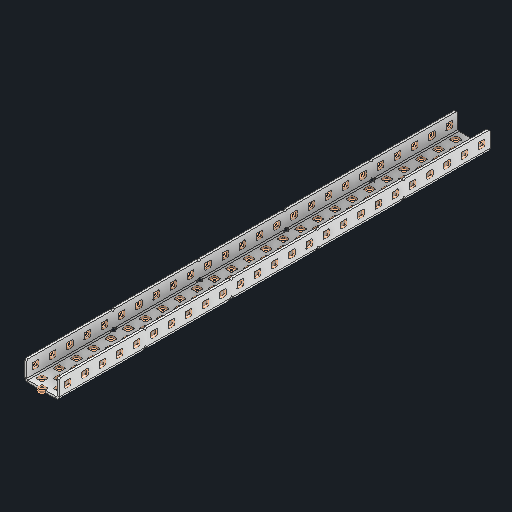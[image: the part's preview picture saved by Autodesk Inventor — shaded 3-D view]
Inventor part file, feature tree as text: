
AUTODESK INVENTOR PART (.ipt)
format: ipt  version: 2024 (Build 280153000, 153)  size: 2,044,928 bytes
history: native  units: in
note: dims shown in document units (in); Inventor stores cm internally (conversion verified against a paired STEP export)
features: other x256, sketch x5, sheet_metal_op x1
ambient origin geometry x8: Origin, YZ Plane, XZ Plane, XY Plane, X Axis, Y Axis, Z Axis, Center Point
bodies: Solid1 (feature_tree)
feature tree (262):
  other  "Alu C 1x2x1x25.ipt"
  other  "Solid1::Alu C 1x2x1x25.ipt"
  other  "TaggingFeature1"
  sketch  "Sketch1"  dims[d0=0.3937in]
  sketch  "Sketch2"  dims[d1=0.0625in]
  sketch  "Sketch3"
  other  "Flange Pattern Sketch"
  sketch  "Sketch9"
  sheet_metal_op  "Body Pattern Sketch"
  other  "Arc Length"
  sketch  "Sketch14"
  other  "Flange Pattern Plane"
  other  "Srf1"
  other  "Srf2"
  other  "Srf3"
  other  "Srf4"
  other  "Srf5"
  other  "Srf6"
  other  "Srf7"
  other  "Srf8"
  other  "Srf9"
  other  "Srf10"
  other  "Srf11"
  other  "Srf12"
  other  "Srf13"
  other  "Srf14"
  other  "Srf15"
  other  "Srf16"
  other  "Srf17"
  other  "Srf18"
  other  "Srf19"
  other  "Srf20"
  other  "Srf21"
  other  "Srf22"
  other  "Srf23"
  other  "Srf24"
  other  "Srf25"
  other  "Srf26"
  other  "Srf27"
  other  "Srf28"
  other  "Srf29"
  other  "Srf30"
  other  "Srf31"
  other  "Srf32"
  other  "Srf33"
  other  "Srf34"
  other  "Srf35"
  other  "Srf36"
  other  "Srf37"
  other  "Srf38"
  other  "Srf39"
  other  "Srf40"
  other  "Srf41"
  other  "Srf42"
  other  "Srf43"
  other  "Srf44"
  other  "Srf45"
  other  "Srf46"
  other  "Srf47"
  other  "Srf48"
  other  "Srf49"
  other  "Srf50"
  other  "Srf51"
  other  "Srf52"
  other  "Srf53"
  other  "Srf54"
  other  "Srf55"
  other  "Srf56"
  other  "Srf57"
  other  "Srf58"
  other  "Srf59"
  other  "Srf60"
  other  "Srf61"
  other  "Srf62"
  other  "Srf63"
  other  "Srf64"
  other  "Srf65"
  other  "Srf66"
  other  "Srf67"
  other  "Srf68"
  other  "Srf69"
  other  "Srf70"
  other  "Srf71"
  other  "Srf72"
  other  "Srf73"
  other  "Srf74"
  other  "Srf75"
  other  "Srf76"
  other  "Srf77"
  other  "Srf78"
  other  "Srf79"
  other  "Srf80"
  other  "Srf81"
  other  "Srf82"
  other  "Srf83"
  other  "Srf84"
  other  "Srf85"
  other  "Srf86"
  other  "Srf87"
  other  "Srf88"
  other  "Srf89"
  other  "Srf90"
  other  "Srf91"
  other  "Srf92"
  other  "Srf93"
  other  "Srf94"
  other  "Srf95"
  other  "Srf96"
  other  "Srf97"
  other  "Srf98"
  other  "Srf99"
  other  "Srf100"
  other  "Srf101"
  other  "Srf102"
  other  "Srf103"
  other  "Srf104"
  other  "Srf105"
  other  "Srf106"
  other  "Srf107"
  other  "Srf108"
  other  "Srf109"
  other  "Srf110"
  other  "Srf111"
  other  "Srf112"
  other  "Srf113"
  other  "Srf114"
  other  "Srf115"
  other  "Srf116"
  other  "Srf117"
  other  "Srf118"
  other  "Srf119"
  other  "Srf120"
  other  "Srf121"
  other  "Srf122"
  other  "Srf123"
  other  "Srf124"
  other  "Srf125"
  other  "Srf1::Derived"
  other  "Srf2::Derived"
  other  "Srf823::Derived"
  other  "Srf824::Derived"
  other  "Srf825::Derived"
  other  "Srf826::Derived"
  other  "Srf827::Derived"
  other  "Srf828::Derived"
  other  "Srf829::Derived"
  other  "Srf922::Derived"
  other  "Srf923::Derived"
  other  "Srf924::Derived"
  other  "Srf925::Derived"
  other  "Srf926::Derived"
  other  "Srf1143::Derived"
  other  "Srf1144::Derived"
  other  "Srf1145::Derived"
  other  "Srf1146::Derived"
  other  "Srf1147::Derived"
  other  "Srf1148::Derived"
  other  "Srf1149::Derived"
  other  "Srf1150::Derived"
  other  "Srf1151::Derived"
  other  "Srf1152::Derived"
  other  "Srf1153::Derived"
  other  "Srf1154::Derived"
  other  "Srf1155::Derived"
  other  "Srf1156::Derived"
  other  "Srf1157::Derived"
  other  "Srf1158::Derived"
  other  "Srf1159::Derived"
  other  "Srf1160::Derived"
  other  "Srf1161::Derived"
  other  "Srf1162::Derived"
  other  "Srf1163::Derived"
  other  "Srf1164::Derived"
  other  "Srf1165::Derived"
  other  "Srf1166::Derived"
  other  "Srf1167::Derived"
  other  "Srf1168::Derived"
  other  "Srf1169::Derived"
  other  "Srf1170::Derived"
  other  "Srf1171::Derived"
  other  "Srf1172::Derived"
  other  "Srf1173::Derived"
  other  "Srf1174::Derived"
  other  "Srf1175::Derived"
  other  "Srf1176::Derived"
  other  "Srf1177::Derived"
  other  "Srf1178::Derived"
  other  "Srf91::Derived"
  other  "Srf92::Derived"
  other  "Srf856::Derived"
  other  "Srf857::Derived"
  other  "Srf858::Derived"
  other  "Srf859::Derived"
  other  "Srf860::Derived"
  other  "Srf861::Derived"
  other  "Srf862::Derived"
  other  "Srf959::Derived"
  other  "Srf960::Derived"
  other  "Srf961::Derived"
  other  "Srf962::Derived"
  other  "Srf963::Derived"
  other  "Srf1199::Derived"
  other  "Srf1200::Derived"
  other  "Srf1201::Derived"
  other  "Srf1202::Derived"
  other  "Srf1203::Derived"
  other  "Srf1204::Derived"
  other  "Srf1205::Derived"
  other  "Srf1206::Derived"
  other  "Srf1207::Derived"
  other  "Srf1208::Derived"
  other  "Srf1209::Derived"
  other  "Srf1210::Derived"
  other  "Srf1211::Derived"
  other  "Srf1212::Derived"
  other  "Srf1213::Derived"
  other  "Srf1214::Derived"
  other  "Srf1215::Derived"
  other  "Srf1216::Derived"
  other  "Srf1217::Derived"
  other  "Srf1218::Derived"
  other  "Srf1219::Derived"
  other  "Srf1220::Derived"
  other  "Srf1221::Derived"
  other  "Srf1222::Derived"
  other  "Srf1223::Derived"
  other  "Srf1224::Derived"
  other  "Srf1225::Derived"
  other  "Srf1226::Derived"
  other  "Srf1227::Derived"
  other  "Srf1228::Derived"
  other  "Srf1229::Derived"
  other  "Srf1230::Derived"
  other  "Srf1231::Derived"
  other  "Srf1232::Derived"
  other  "Srf1233::Derived"
  other  "Srf1234::Derived"
  other  "Srf786::Derived"
  other  "Srf889::Derived"
  other  "Srf890::Derived"
  other  "Srf891::Derived"
  other  "Srf892::Derived"
  other  "Srf893::Derived"
  other  "Srf894::Derived"
  other  "Srf895::Derived"
  other  "Srf896::Derived"
  other  "Srf996::Derived"
  other  "Srf997::Derived"
  other  "Srf998::Derived"
  other  "Srf999::Derived"
  other  "Srf1000::Derived"
  other  "Srf1255::Derived"
  other  "Srf1256::Derived"
  other  "Srf1257::Derived"
  other  "Srf1258::Derived"
  other  "Srf1259::Derived"
  other  "Srf1260::Derived"
  other  "Srf1261::Derived"
  other  "Srf1262::Derived"
  other  "Srf1263::Derived"
  other  "Srf1264::Derived"
  other  "Srf1265::Derived"
